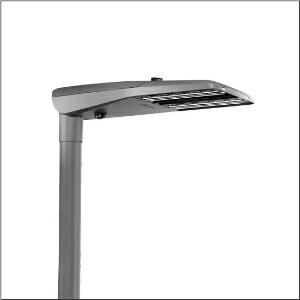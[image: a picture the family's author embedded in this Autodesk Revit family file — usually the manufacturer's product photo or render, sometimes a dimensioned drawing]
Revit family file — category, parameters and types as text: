
# Revit family: streetlight_sl_11_iq_midi___st1_0a_5xc3m51y08me_5fc7
name_source: partatom
category: Lighting Fixtures
units: mm (PartAtom-declared; Revit-internal decimal feet)

## family parameters
Cut with Voids When Loaded = No
Host = Face
Light Source = No
Part Type = Normal
Room Calculation Point = No
Round Connector Dimension = Use Diameter
Shared = No

## types (1)
- --- (1 x LED, 17540 lm, 122.7 W, 3000K)
    Apparent Load = 123 VA
    CIE Flux Codes = 33 66 96 100 100
    Color Rendering = 70
    Color Temperature = 3000K
    Default Elevation = 1800 mm
    Description = Streetlight SL 11 iQ midi, mast luminaire, primary light control with 3 zone facetted reflector, of plastic, silver coated, highly specular, primary optical cover: cover, of PMMA, transparent, light distribution: ST1.0a, light emission: direct distribution, primary light characteristic: asymmetric, installation type: post-top, side-entry, LED, High Power LED, rated luminous flux: 17.540lm, luminous efficacy: 143lm/W, light colour: 730, colour temperature: 3000K, control: presetting dimming logarithmic, Street-Remote, Auto-Match, Temp-Guard, Lumen-Switch, Night-Set, Smart-Wire, Light-Fading, Desk-Remote (wireless, voltage-free reading and setting of iQ features in the workshop via application-optimized NFC function/RFID function), optimised constant luminous flux control (CLO 2.0), with cable H07RN-F 5x 1.5mm², mains connection: 230..240V, AC, 50/60Hz, connection cable pre-assembled, cable length: 12,5m, start of lifetime: 123W, end of service life: 130W, reduction: 56W, luminaire housing, of diecast aluminium, powder-coated, Siteco® metallic grey (DB 702S), please order mast flange separately, inclination adjustable without tools: 0°, 5°, 10°, 15° (post-top) | 0°, -5°, -10°, -15° (side-entry), sealing non-destructively replaceable, multi-level sealing system, length: 780mm, width: 376mm, height: 118mm, mast flange for spigot size: 42mm (side-entry): 5XC10008XM4, 60/48mm (side-entry/post-top): 5XC10108XM2, 76/60mm (side-entry/post-top): 5XC10108XM1, equipment: Power, Smart Interface below and above, protection rating (complete): IP66, insulation class (complete): insulation class II (safety insulation), certification: CE, ENEC, VDE, UKCA, impact resistance: IK09, permissible operating ambient temperature for outdoor applications: -25..+50°C, standard-compliant lighting for roads and squares, Environmental Product Declaration (EPD) tested and certified by an independent institute, packaging unit: 1 piece

Light Distribution: ST1.0a
    Height = 118 mm
    Lamp = 1 x LED
    Lamp Light Flux = 17540 lm
    Lamp Power = 122.7 W
    Lamp count = 1
    Length = 780 mm
    Luminous efficacy = 143 lm/W
    Manufacturer = Siteco
    ModVariant = No
    Model = 5XC3M51Y08ME
    Number of Poles = 1
    OnlyDefault = Yes
    Power Factor = 1
    Product Name = Streetlight SL 11 iQ midi | ST1.0a
    Product group = mast luminaire | pylon top
    ProductGroupID = 6100
    Protection Class = Protection class II
    Protection Degree = IP 66
    RLX_Detail_Level = 1
    RLX_Emergency_Light_Flux = 0 lm
    RLX_Emergency_Type = 0
    RLX_Emergency_Type_DB = No
    RlxData = <blob elided: 69285 chars, md5=42ec43b7>
    Socket = socket
    Standby Power = 0 W
    System Light Flux = 17540 lm
    System Power = 123 W
    Type Comments = factory setting: luminous flux: 100 % | dim-lin: 254 | 553 mA
    Type Image = l_1004429.jpg
    URL = http://relux.com
    VarID = @adj_039379
    Voltage = 0 V
    Weight = 0.00 kg
    Width = 376 mm

## geometry (parser evidence)
native form markers: Blend x4, Sweep x12
no freeform markers — native parametric forms only
